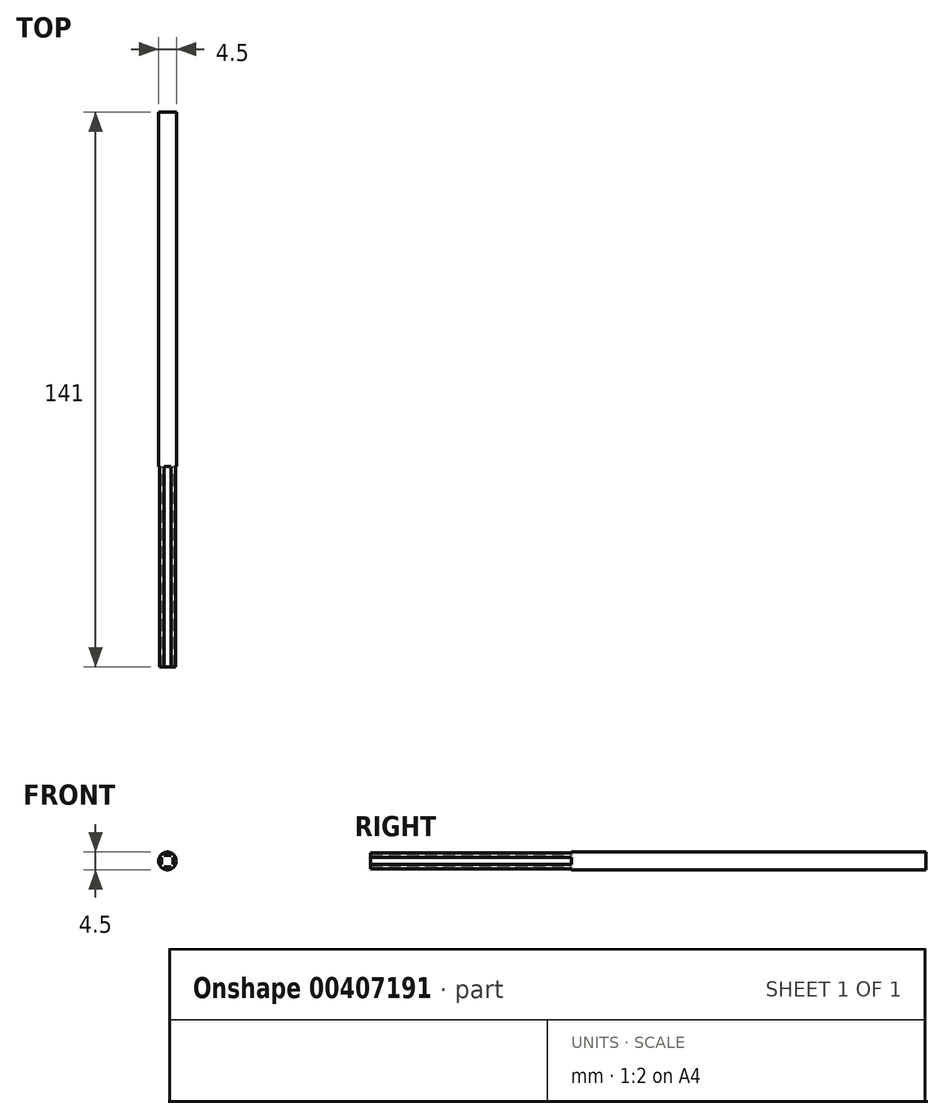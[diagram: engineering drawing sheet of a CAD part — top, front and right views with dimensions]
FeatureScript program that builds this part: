
annotation { "Feature Type Name" : "Feature", "Feature Type Description" : "" }
export const myFeature = defineFeature(function(context is Context, id is Id, definition is map)
    precondition{}
    {
        {
            var Q0;
            Q0=qCreatedBy(makeId("Front.planeOp"),FACE);
            var sketch = newSketch(context, id + "F0", { "sketchPlane" : qUnion([Q0])});
            skCircle(sketch, "E0", {"center": v(0, 0) * mm, "radius": 2.25 * mm});
            skLineSegment(sketch, "E1.bottom", {"start": v(0, 2.25) * mm, "end": v(-0.9, 2.25) * mm});
            skLineSegment(sketch, "E1.top", {"start": v(0, 1.45) * mm, "end": v(-0.9, 1.45) * mm});
            skLineSegment(sketch, "E1.right", {"start": v(-0.9, 2.25) * mm, "end": v(-0.9, 1.45) * mm});
            skLineSegment(sketch, "E2.top", {"start": v(-2.25, 0.9) * mm, "end": v(-1.45, 0.9) * mm});
            skLineSegment(sketch, "E2.left", {"start": v(-2.25, 0) * mm, "end": v(-2.25, 0.9) * mm});
            skLineSegment(sketch, "E2.right", {"start": v(-1.45, 0) * mm, "end": v(-1.45, 0.9) * mm});
            skLineSegment(sketch, "E3.MirrorCS", {"start": v(-2.25, -0.9) * mm, "end": v(-1.45, -0.9) * mm});
            skLineSegment(sketch, "E4.MirrorCS", {"start": v(-2.25, 0) * mm, "end": v(-2.25, -0.9) * mm});
            skLineSegment(sketch, "E5.MirrorCS", {"start": v(-1.45, 0) * mm, "end": v(-1.45, -0.9) * mm});
            skLineSegment(sketch, "E6.MirrorCS", {"start": v(0, -1.45) * mm, "end": v(-0.9, -1.45) * mm});
            skLineSegment(sketch, "E7.MirrorCS", {"start": v(-0.9, -2.25) * mm, "end": v(-0.9, -1.45) * mm});
            skLineSegment(sketch, "E8.MirrorCS", {"start": v(0, -2.25) * mm, "end": v(-0.9, -2.25) * mm});
            skLineSegment(sketch, "E9.MirrorCS", {"start": v(0, 2.25) * mm, "end": v(0.9, 2.25) * mm});
            skLineSegment(sketch, "E10.MirrorCS", {"start": v(0.9, 2.25) * mm, "end": v(0.9, 1.45) * mm});
            skLineSegment(sketch, "E11.MirrorCS", {"start": v(0, 1.45) * mm, "end": v(0.9, 1.45) * mm});
            skLineSegment(sketch, "E12.MirrorCS", {"start": v(2.25, 0) * mm, "end": v(2.25, 0.9) * mm});
            skLineSegment(sketch, "E13.MirrorCS", {"start": v(2.25, 0) * mm, "end": v(2.25, -0.9) * mm});
            skLineSegment(sketch, "E14.MirrorCS", {"start": v(2.25, -0.9) * mm, "end": v(1.45, -0.9) * mm});
            skLineSegment(sketch, "E15.MirrorCS", {"start": v(1.45, 0) * mm, "end": v(1.45, -0.9) * mm});
            skLineSegment(sketch, "E16.MirrorCS", {"start": v(1.45, 0) * mm, "end": v(1.45, 0.9) * mm});
            skLineSegment(sketch, "E17.MirrorCS", {"start": v(2.25, 0.9) * mm, "end": v(1.45, 0.9) * mm});
            skLineSegment(sketch, "E18.MirrorCS", {"start": v(0, -1.45) * mm, "end": v(0.9, -1.45) * mm});
            skLineSegment(sketch, "E19.MirrorCS", {"start": v(0.9, -2.25) * mm, "end": v(0.9, -1.45) * mm});
            skLineSegment(sketch, "E20.MirrorCS", {"start": v(0, -2.25) * mm, "end": v(0.9, -2.25) * mm});
            skPoint(sketch, "E21.MirrorCS.end.orphan", {"position": v(0, -1.45) * mm});
            skPoint(sketch, "E21.MirrorCS.start.orphan", {"position": v(0, -2.25) * mm});
            skLineSegment(sketch, "E22", {"start": v(0, 3.57) * mm, "end": v(0, -2.78) * mm, "construction": true});
            skSolve(sketch);
        }
        {
            var Q0;
            {var subQ7=sQuery(id+"F0.wireOp",EDGE,"E1.top");Q0=makeQuery(id+"F0.imprint","IMPRINT",FACE,{"disambiguationData":[TD([[makeQuery(id+"F0.imprint","IMPRINT",EDGE,{"derivedFrom":subQ7}),1.0]])]});}
            extrude(context, id + "F1", {"entities" : qUnion([Q0]), "depth" : 51 * mm});
        }
        {
            var Q0;
            {var subQ7=sQuery(id+"F0.wireOp",EDGE,"E1.top");Q0=makeQuery(id+"F0.imprint","IMPRINT",FACE,{"disambiguationData":[TD([[makeQuery(id+"F0.imprint","IMPRINT",EDGE,{"derivedFrom":subQ7}),1.0]])]});}
            var Q1;
            {var subQ1=sQuery(id+"F0.wireOp",EDGE,"E1.top");Q1=makeQuery(id+"F0.imprint","IMPRINT",FACE,{"disambiguationData":[TD([[makeQuery(id+"F0.imprint","IMPRINT",EDGE,{"derivedFrom":subQ1}),-1.0]])]});}
            var Q2;
            {var subQ0=sQuery(id+"F0.wireOp",EDGE,"E2.right");Q2=makeQuery(id+"F0.imprint","IMPRINT",FACE,{"disambiguationData":[TD([[makeQuery(id+"F0.imprint","IMPRINT",EDGE,{"derivedFrom":subQ0}),1.0]])]});}
            var Q3;
            {var subQ1=sQuery(id+"F0.wireOp",EDGE,"E6.MirrorCS");Q3=makeQuery(id+"F0.imprint","IMPRINT",FACE,{"disambiguationData":[TD([[makeQuery(id+"F0.imprint","IMPRINT",EDGE,{"derivedFrom":subQ1}),1.0]])]});}
            var Q4;
            {var subQ0=sQuery(id+"F0.wireOp",EDGE,"E15.MirrorCS");Q4=makeQuery(id+"F0.imprint","IMPRINT",FACE,{"disambiguationData":[TD([[makeQuery(id+"F0.imprint","IMPRINT",EDGE,{"derivedFrom":subQ0}),1.0]])]});}
            extrude(context, id + "F2", {"entities" : qUnion([Q0, Q1, Q2, Q3, Q4]), "operationType" : NewBodyOperationType.ADD, "oppositeDirection" : true, "depth" : 90 * mm});
        }
    });
